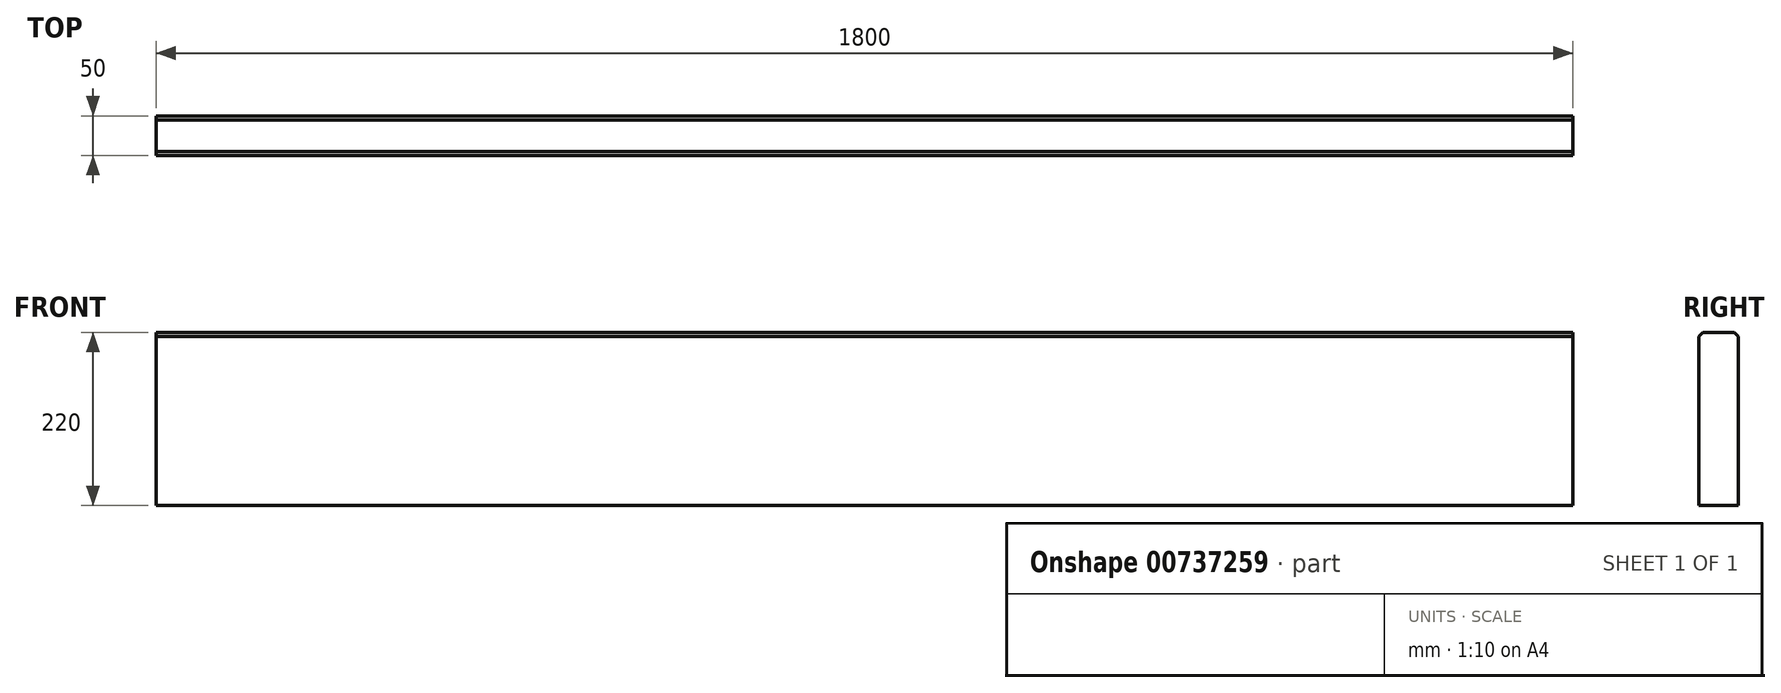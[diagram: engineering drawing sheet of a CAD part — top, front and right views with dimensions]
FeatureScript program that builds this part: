
annotation { "Feature Type Name" : "Feature", "Feature Type Description" : "" }
export const myFeature = defineFeature(function(context is Context, id is Id, definition is map)
    precondition{}
    {
        {
            var Q0;
            Q0=qCreatedBy(makeId("Front.planeOp"),FACE);
            var sketch = newSketch(context, id + "F0", { "sketchPlane" : qUnion([Q0])});
            skLineSegment(sketch, "E0.bottom", {"start": v(0, 0) * mm, "end": v(1800, 0) * mm});
            skLineSegment(sketch, "E0.top", {"start": v(0, 220) * mm, "end": v(1800, 220) * mm});
            skLineSegment(sketch, "E0.left", {"start": v(0, 0) * mm, "end": v(0, 220) * mm});
            skLineSegment(sketch, "E0.right", {"start": v(1800, 0) * mm, "end": v(1800, 220) * mm});
            skSolve(sketch);
        }
        {
            var Q0;
            Q0 = qSketchRegion(id + "F0", true);
            extrude(context, id + "F1", {"entities" : qUnion([Q0]), "depth" : 50 * mm, "offsetDistance" : 25 * mm});
        }
        {
            var Q0;
            Q0=makeQuery(id+"F1.opExtrude","CAP_EDGE",EDGE,{"disambiguationData":[OSD([sQuery(id+"F0.wireOp",EDGE,"E0.top")])],"isStart":false});
            var Q1;
            Q1=makeQuery(id+"F1.opExtrude","CAP_EDGE",EDGE,{"disambiguationData":[OSD([sQuery(id+"F0.wireOp",EDGE,"E0.top")])],"isStart":true});
            chamfer(context, id + "F2", {"entities" : qUnion([Q0, Q1]), "width" : 5 * mm, "tangentPropagation" : true});
        }
    });
